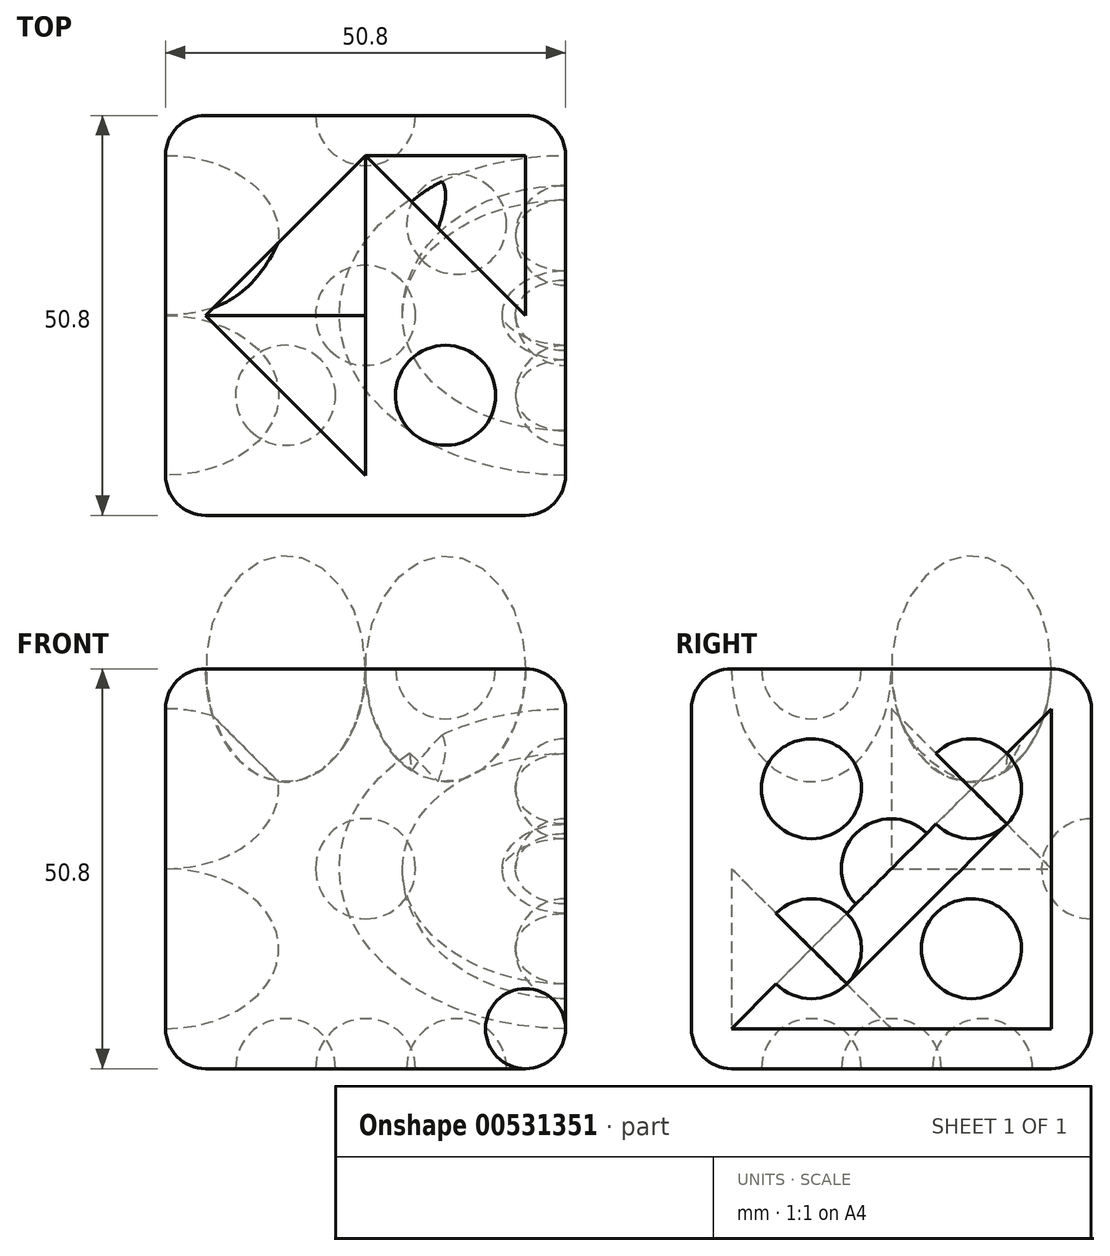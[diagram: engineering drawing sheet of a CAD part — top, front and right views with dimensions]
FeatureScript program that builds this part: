
annotation { "Feature Type Name" : "Feature", "Feature Type Description" : "" }
export const myFeature = defineFeature(function(context is Context, id is Id, definition is map)
    precondition{}
    {
        {
            var Q0;
            Q0=qCreatedBy(makeId("Front.planeOp"),FACE);
            var sketch = newSketch(context, id + "F0", { "sketchPlane" : qUnion([Q0])});
            skLineSegment(sketch, "E0", {"start": v(0, 0) * mm, "end": v(50.8, 0) * mm});
            skLineSegment(sketch, "E1", {"start": v(50.8, 0) * mm, "end": v(50.8, 50.8) * mm});
            skLineSegment(sketch, "E2", {"start": v(50.8, 50.8) * mm, "end": v(0, 50.8) * mm});
            skLineSegment(sketch, "E3", {"start": v(0, 50.8) * mm, "end": v(0, 0) * mm});
            skSolve(sketch);
        }
        {
            var Q0;
            Q0 = qSketchRegion(id + "F0", true);
            extrude(context, id + "F1", {"entities" : qUnion([Q0]), "depth" : 50.8 * mm, "offsetDistance" : 25.4 * mm});
        }
        {
            var Q0;
            Q0=makeQuery(id+"F1.opExtrude","CAP_EDGE",EDGE,{"disambiguationData":[OSD([sQuery(id+"F0.wireOp",EDGE,"E2")])],"isStart":false});
            var Q1;
            Q1=makeQuery(id+"F1.opExtrude","SWEPT_EDGE",EDGE,{"disambiguationData":[OSD([sQuery(id+"F0.wireOp",EDGE,"E1"),sQuery(id+"F0.wireOp",EDGE,"E2")])]});
            var Q2;
            Q2=makeQuery(id+"F1.opExtrude","CAP_EDGE",EDGE,{"disambiguationData":[OSD([sQuery(id+"F0.wireOp",EDGE,"E0")])],"isStart":false});
            var Q3;
            Q3=makeQuery(id+"F1.opExtrude","SWEPT_EDGE",EDGE,{"disambiguationData":[OSD([sQuery(id+"F0.wireOp",EDGE,"E0"),sQuery(id+"F0.wireOp",EDGE,"E1")])]});
            var Q4;
            Q4=makeQuery(id+"F1.opExtrude","CAP_EDGE",EDGE,{"disambiguationData":[OSD([sQuery(id+"F0.wireOp",EDGE,"E1")])],"isStart":false});
            var Q5;
            Q5=makeQuery(id+"F1.opExtrude","CAP_EDGE",EDGE,{"disambiguationData":[OSD([sQuery(id+"F0.wireOp",EDGE,"E1")])],"isStart":true});
            var Q6;
            Q6=makeQuery(id+"F1.opExtrude","CAP_EDGE",EDGE,{"disambiguationData":[OSD([sQuery(id+"F0.wireOp",EDGE,"E3")])],"isStart":false});
            var Q7;
            Q7=makeQuery(id+"F1.opExtrude","SWEPT_EDGE",EDGE,{"disambiguationData":[OSD([sQuery(id+"F0.wireOp",EDGE,"E2"),sQuery(id+"F0.wireOp",EDGE,"E3")])]});
            var Q8;
            Q8=makeQuery(id+"F1.opExtrude","CAP_EDGE",EDGE,{"disambiguationData":[OSD([sQuery(id+"F0.wireOp",EDGE,"E2")])],"isStart":true});
            var Q9;
            Q9=makeQuery(id+"F1.opExtrude","CAP_EDGE",EDGE,{"disambiguationData":[OSD([sQuery(id+"F0.wireOp",EDGE,"E3")])],"isStart":true});
            var Q10;
            Q10=makeQuery(id+"F1.opExtrude","SWEPT_EDGE",EDGE,{"disambiguationData":[OSD([sQuery(id+"F0.wireOp",EDGE,"E0"),sQuery(id+"F0.wireOp",EDGE,"E3")])]});
            var Q11;
            Q11=makeQuery(id+"F1.opExtrude","CAP_EDGE",EDGE,{"disambiguationData":[OSD([sQuery(id+"F0.wireOp",EDGE,"E0")])],"isStart":true});
            fillet(context, id + "F2", {"entities" : qUnion([Q0, Q1, Q2, Q3, Q4, Q5, Q6, Q7, Q8, Q9, Q10, Q11]), "radius" : 5.08 * mm, "tangentPropagation" : true, "allowEdgeOverflow" : false});
        }
        {
            var Q0;
            Q0=makeQuery(id+"F1.opExtrude","CAP_FACE",FACE,{"disambiguationData":[OSD([sQuery(id+"F0.wireOp",EDGE,"E0"),sQuery(id+"F0.wireOp",EDGE,"E1"),sQuery(id+"F0.wireOp",EDGE,"E2"),sQuery(id+"F0.wireOp",EDGE,"E3")])],"isStart":false});
            var sketch = newSketch(context, id + "F3", { "sketchPlane" : qUnion([Q0])});
            skLineSegment(sketch, "E4", {"start": v(5.08, 45.72) * mm, "end": v(45.72, 5.08) * mm});
            skLineSegment(sketch, "E5", {"start": v(5.08, 5.08) * mm, "end": v(45.72, 45.72) * mm});
            skLineSegment(sketch, "E6", {"start": v(25.4, 45.72) * mm, "end": v(25.4, 5.08) * mm});
            skLineSegment(sketch, "E7", {"start": v(5.08, 25.4) * mm, "end": v(45.72, 25.4) * mm});
            skLineSegment(sketch, "E8", {"start": v(5.08, 25.4) * mm, "end": v(25.4, 45.72) * mm});
            skLineSegment(sketch, "E9", {"start": v(25.4, 45.72) * mm, "end": v(45.72, 25.4) * mm});
            skLineSegment(sketch, "E10", {"start": v(5.08, 25.4) * mm, "end": v(25.4, 5.08) * mm});
            skLineSegment(sketch, "E11", {"start": v(45.72, 25.4) * mm, "end": v(25.4, 5.08) * mm});
            skCircle(sketch, "E12", {"center": v(25.4, 25.4) * mm, "radius": 6.35 * mm});
            skSolve(sketch);
        }
        {
            var Q0;
            Q0=makeQuery(id+"F1.opExtrude","SWEPT_FACE",FACE,{"disambiguationData":[OSD([sQuery(id+"F0.wireOp",EDGE,"E3")])]});
            var sketch = newSketch(context, id + "F4", { "sketchPlane" : qUnion([Q0])});
            skLineSegment(sketch, "E13", {"start": v(5.08, 45.72) * mm, "end": v(45.72, 5.08) * mm});
            skLineSegment(sketch, "E14", {"start": v(5.08, 5.08) * mm, "end": v(45.72, 45.72) * mm});
            skLineSegment(sketch, "E15", {"start": v(5.08, 25.4) * mm, "end": v(45.72, 25.4) * mm});
            skLineSegment(sketch, "E16", {"start": v(25.4, 45.72) * mm, "end": v(25.4, 5.08) * mm});
            skLineSegment(sketch, "E17", {"start": v(5.08, 25.4) * mm, "end": v(25.4, 45.72) * mm});
            skLineSegment(sketch, "E18", {"start": v(25.4, 5.08) * mm, "end": v(45.72, 25.4) * mm});
            skCircle(sketch, "E19", {"center": v(15.24, 35.56) * mm, "radius": 6.35 * mm});
            skCircle(sketch, "E20", {"center": v(35.56, 15.24) * mm, "radius": 6.35 * mm});
            skSolve(sketch);
        }
        {
            var Q0;
            {var subQ0=sQuery(id+"F4.wireOp",EDGE,"E19");var subQ1=sQuery(id+"F4.wireOp",EDGE,"E13");var subQ2=makeQuery(id+"F4.imprint","INTERSECT",VERTEX,{"disambiguationData":[OD(0.0)],"derivedFrom":[subQ1,subQ0]});Q0=makeQuery(id+"F4.imprint","IMPRINT",FACE,{"disambiguationData":[TD([[makeQuery(id+"F4.imprint","IMPRINT",EDGE,{"disambiguationData":[TD([[subQ2,-1.0]])],"derivedFrom":subQ1}),1.0]])]});}
            var Q1;
            {var subQ0=sQuery(id+"F4.wireOp",EDGE,"E17");var subQ1=sQuery(id+"F4.wireOp",EDGE,"E13");var subQ2=makeQuery(id+"F4.imprint","INTERSECT",VERTEX,{"derivedFrom":[subQ1,subQ0]});Q1=makeQuery(id+"F4.imprint","IMPRINT",FACE,{"disambiguationData":[TD([[makeQuery(id+"F4.imprint","IMPRINT",EDGE,{"disambiguationData":[TD([[subQ2,-1.0]])],"derivedFrom":subQ1}),1.0]])]});}
            var Q2;
            {var subQ0=sQuery(id+"F4.wireOp",EDGE,"E20");var subQ1=sQuery(id+"F4.wireOp",EDGE,"E13");var subQ2=makeQuery(id+"F4.imprint","INTERSECT",VERTEX,{"disambiguationData":[OD(0.0)],"derivedFrom":[subQ1,subQ0]});Q2=makeQuery(id+"F4.imprint","IMPRINT",FACE,{"disambiguationData":[TD([[makeQuery(id+"F4.imprint","IMPRINT",EDGE,{"disambiguationData":[TD([[subQ2,-1.0]])],"derivedFrom":subQ1}),1.0]])]});}
            var Q3;
            {var subQ0=sQuery(id+"F4.wireOp",EDGE,"E18");var subQ1=sQuery(id+"F4.wireOp",EDGE,"E13");var subQ2=makeQuery(id+"F4.imprint","INTERSECT",VERTEX,{"derivedFrom":[subQ1,subQ0]});Q3=makeQuery(id+"F4.imprint","IMPRINT",FACE,{"disambiguationData":[TD([[makeQuery(id+"F4.imprint","IMPRINT",EDGE,{"disambiguationData":[TD([[subQ2,-1.0]])],"derivedFrom":subQ1}),1.0]])]});}
            var Q4;
            Q4=sQuery(id+"F4.wireOp",EDGE,"E13");
            revolve(context, id + "F5", {"operationType" : NewBodyOperationType.REMOVE, "entities" : qUnion([Q0, Q1, Q2, Q3]), "axis" : qUnion([Q4]), "revolveType" : RevolveType.FULL, "oppositeDirection" : true});
        }
        {
            var Q0;
            Q0=makeQuery(id+"F1.opExtrude","SWEPT_FACE",FACE,{"disambiguationData":[OSD([sQuery(id+"F0.wireOp",EDGE,"E0")])]});
            var sketch = newSketch(context, id + "F6", { "sketchPlane" : qUnion([Q0])});
            skLineSegment(sketch, "E21", {"start": v(5.08, 45.72) * mm, "end": v(45.72, 5.08) * mm});
            skCircle(sketch, "E22", {"center": v(15.24, 35.56) * mm, "radius": 6.35 * mm});
            skCircle(sketch, "E23", {"center": v(25.4, 25.4) * mm, "radius": 6.35 * mm});
            skCircle(sketch, "E24", {"center": v(36.97, 13.83) * mm, "radius": 6.35 * mm});
            skSolve(sketch);
        }
        {
            var Q0;
            {var subQ0=sQuery(id+"F6.wireOp",EDGE,"E22");var subQ1=sQuery(id+"F6.wireOp",EDGE,"E21");var subQ2=makeQuery(id+"F6.imprint","INTERSECT",VERTEX,{"disambiguationData":[OD(0.0)],"derivedFrom":[subQ1,subQ0]});Q0=makeQuery(id+"F6.imprint","IMPRINT",FACE,{"disambiguationData":[TD([[makeQuery(id+"F6.imprint","IMPRINT",EDGE,{"disambiguationData":[TD([[subQ2,-1.0]])],"derivedFrom":subQ1}),-1.0]])]});}
            var Q1;
            {var subQ0=sQuery(id+"F6.wireOp",EDGE,"E23");var subQ1=sQuery(id+"F6.wireOp",EDGE,"E21");var subQ2=makeQuery(id+"F6.imprint","INTERSECT",VERTEX,{"disambiguationData":[OD(0.0)],"derivedFrom":[subQ1,subQ0]});Q1=makeQuery(id+"F6.imprint","IMPRINT",FACE,{"disambiguationData":[TD([[makeQuery(id+"F6.imprint","IMPRINT",EDGE,{"disambiguationData":[TD([[subQ2,-1.0]])],"derivedFrom":subQ1}),-1.0]])]});}
            var Q2;
            {var subQ0=sQuery(id+"F6.wireOp",EDGE,"E24");var subQ1=sQuery(id+"F6.wireOp",EDGE,"E21");var subQ2=makeQuery(id+"F6.imprint","INTERSECT",VERTEX,{"disambiguationData":[OD(0.0)],"derivedFrom":[subQ1,subQ0]});Q2=makeQuery(id+"F6.imprint","IMPRINT",FACE,{"disambiguationData":[TD([[makeQuery(id+"F6.imprint","IMPRINT",EDGE,{"disambiguationData":[TD([[subQ2,-1.0]])],"derivedFrom":subQ1}),-1.0]])]});}
            var Q3;
            Q3=sQuery(id+"F6.wireOp",EDGE,"E21");
            revolve(context, id + "F7", {"operationType" : NewBodyOperationType.REMOVE, "entities" : qUnion([Q0, Q1, Q2]), "axis" : qUnion([Q3]), "revolveType" : RevolveType.FULL, "oppositeDirection" : true});
        }
        {
            var Q0;
            Q0=makeQuery(id+"F1.opExtrude","SWEPT_FACE",FACE,{"disambiguationData":[OSD([sQuery(id+"F0.wireOp",EDGE,"E2")])]});
            var sketch = newSketch(context, id + "F8", { "sketchPlane" : qUnion([Q0])});
            skLineSegment(sketch, "E25", {"start": v(5.08, -5.08) * mm, "end": v(45.72, -45.72) * mm});
            skLineSegment(sketch, "E26", {"start": v(5.08, -45.72) * mm, "end": v(45.72, -5.08) * mm});
            skLineSegment(sketch, "E27", {"start": v(25.4, -5.08) * mm, "end": v(25.4, -45.72) * mm});
            skLineSegment(sketch, "E28", {"start": v(5.08, -25.4) * mm, "end": v(45.72, -25.4) * mm});
            skLineSegment(sketch, "E29", {"start": v(25.4, -5.08) * mm, "end": v(45.72, -25.4) * mm});
            skLineSegment(sketch, "E30", {"start": v(45.72, -25.4) * mm, "end": v(25.4, -45.72) * mm});
            skLineSegment(sketch, "E31", {"start": v(5.08, -25.4) * mm, "end": v(25.4, -45.72) * mm});
            skLineSegment(sketch, "E32", {"start": v(5.08, -25.4) * mm, "end": v(25.4, -5.08) * mm});
            skCircle(sketch, "E33", {"center": v(15.24, -15.24) * mm, "radius": 6.35 * mm});
            skCircle(sketch, "E34", {"center": v(35.56, -15.24) * mm, "radius": 6.35 * mm});
            skCircle(sketch, "E35", {"center": v(15.24, -35.56) * mm, "radius": 6.35 * mm});
            skCircle(sketch, "E36", {"center": v(35.56, -35.56) * mm, "radius": 6.35 * mm});
            skSolve(sketch);
        }
        {
            var Q0;
            {var subQ0=sQuery(id+"F8.wireOp",EDGE,"E33");var subQ1=sQuery(id+"F8.wireOp",EDGE,"E25");var subQ2=makeQuery(id+"F8.imprint","INTERSECT",VERTEX,{"disambiguationData":[OD(0.0)],"derivedFrom":[subQ1,subQ0]});Q0=makeQuery(id+"F8.imprint","IMPRINT",FACE,{"disambiguationData":[TD([[makeQuery(id+"F8.imprint","IMPRINT",EDGE,{"disambiguationData":[TD([[subQ2,-1.0]])],"derivedFrom":subQ1}),1.0]])]});}
            var Q1;
            {var subQ0=sQuery(id+"F8.wireOp",EDGE,"E32");var subQ1=sQuery(id+"F8.wireOp",EDGE,"E25");var subQ2=makeQuery(id+"F8.imprint","INTERSECT",VERTEX,{"derivedFrom":[subQ1,subQ0]});Q1=makeQuery(id+"F8.imprint","IMPRINT",FACE,{"disambiguationData":[TD([[makeQuery(id+"F8.imprint","IMPRINT",EDGE,{"disambiguationData":[TD([[subQ2,-1.0]])],"derivedFrom":subQ1}),1.0]])]});}
            var Q2;
            {var subQ0=sQuery(id+"F8.wireOp",EDGE,"E36");var subQ1=sQuery(id+"F8.wireOp",EDGE,"E25");var subQ2=makeQuery(id+"F8.imprint","INTERSECT",VERTEX,{"disambiguationData":[OD(0.0)],"derivedFrom":[subQ1,subQ0]});Q2=makeQuery(id+"F8.imprint","IMPRINT",FACE,{"disambiguationData":[TD([[makeQuery(id+"F8.imprint","IMPRINT",EDGE,{"disambiguationData":[TD([[subQ2,-1.0]])],"derivedFrom":subQ1}),1.0]])]});}
            var Q3;
            {var subQ0=sQuery(id+"F8.wireOp",EDGE,"E30");var subQ1=sQuery(id+"F8.wireOp",EDGE,"E25");var subQ2=makeQuery(id+"F8.imprint","INTERSECT",VERTEX,{"derivedFrom":[subQ1,subQ0]});Q3=makeQuery(id+"F8.imprint","IMPRINT",FACE,{"disambiguationData":[TD([[makeQuery(id+"F8.imprint","IMPRINT",EDGE,{"disambiguationData":[TD([[subQ2,-1.0]])],"derivedFrom":subQ1}),1.0]])]});}
            var Q4;
            Q4=sQuery(id+"F8.wireOp",EDGE,"E25");
            revolve(context, id + "F9", {"operationType" : NewBodyOperationType.REMOVE, "entities" : qUnion([Q0, Q1, Q2, Q3]), "axis" : qUnion([Q4]), "revolveType" : RevolveType.FULL, "oppositeDirection" : true});
        }
        {
            var Q0;
            Q0=makeQuery(id+"F1.opExtrude","CAP_FACE",FACE,{"disambiguationData":[OSD([sQuery(id+"F0.wireOp",EDGE,"E0"),sQuery(id+"F0.wireOp",EDGE,"E1"),sQuery(id+"F0.wireOp",EDGE,"E2"),sQuery(id+"F0.wireOp",EDGE,"E3")])],"isStart":true});
            var sketch = newSketch(context, id + "F10", { "sketchPlane" : qUnion([Q0])});
            skLineSegment(sketch, "E37", {"start": v(-25.4, 45.72) * mm, "end": v(-25.4, 31.75) * mm});
            skArc(sketch, "E38", {"start": v(-31.75, 25.4) * mm, "mid": v(-25.4, 19.05) * mm, "end": v(-19.05, 25.4) * mm});
            skLineSegment(sketch, "E39", {"start": v(-5.08, 25.4) * mm, "end": v(-45.72, 25.4) * mm});
            skLineSegment(sketch, "E40.trimOffspring", {"start": v(-25.4, 19.05) * mm, "end": v(-25.4, 5.08) * mm});
            skSolve(sketch);
        }
        {
            var Q0;
            {var subQ0=sQuery(id+"F10.wireOp",EDGE,"E39");var subQ1=sQuery(id+"F10.wireOp",EDGE,"E38");var subQ2=makeQuery(id+"F10.imprint","INTERSECT",VERTEX,{"disambiguationData":[OD(0.0)],"derivedFrom":[subQ1,subQ0]});Q0=makeQuery(id+"F10.imprint","IMPRINT",FACE,{"disambiguationData":[TD([[makeQuery(id+"F10.imprint","IMPRINT",EDGE,{"disambiguationData":[TD([[subQ2,-1.0]])],"derivedFrom":subQ1}),1.0]])]});}
            var Q1;
            Q1=sQuery(id+"F10.wireOp",EDGE,"E39");
            revolve(context, id + "F11", {"operationType" : NewBodyOperationType.REMOVE, "entities" : qUnion([Q0]), "axis" : qUnion([Q1]), "revolveType" : RevolveType.FULL, "oppositeDirection" : true});
        }
        {
            var Q0;
            Q0=makeQuery(id+"F1.opExtrude","SWEPT_FACE",FACE,{"disambiguationData":[OSD([sQuery(id+"F0.wireOp",EDGE,"E1")])]});
            var sketch = newSketch(context, id + "F12", { "sketchPlane" : qUnion([Q0])});
            skLineSegment(sketch, "E41", {"start": v(-45.72, 45.72) * mm, "end": v(-5.08, 5.08) * mm});
            skLineSegment(sketch, "E42", {"start": v(-45.72, 5.08) * mm, "end": v(-5.08, 45.72) * mm});
            skCircle(sketch, "E43", {"center": v(-25.4, 25.4) * mm, "radius": 6.35 * mm});
            skCircle(sketch, "E44", {"center": v(-35.56, 35.56) * mm, "radius": 6.35 * mm});
            skCircle(sketch, "E45", {"center": v(-15.24, 35.56) * mm, "radius": 6.35 * mm});
            skCircle(sketch, "E46", {"center": v(-35.56, 15.24) * mm, "radius": 6.35 * mm});
            skCircle(sketch, "E47", {"center": v(-15.24, 15.24) * mm, "radius": 6.35 * mm});
            skSolve(sketch);
        }
        {
            var Q0;
            {var subQ0=sQuery(id+"F12.wireOp",EDGE,"E44");var subQ1=sQuery(id+"F12.wireOp",EDGE,"E41");var subQ2=makeQuery(id+"F12.imprint","INTERSECT",VERTEX,{"disambiguationData":[OD(0.0)],"derivedFrom":[subQ1,subQ0]});Q0=makeQuery(id+"F12.imprint","IMPRINT",FACE,{"disambiguationData":[TD([[makeQuery(id+"F12.imprint","IMPRINT",EDGE,{"disambiguationData":[TD([[subQ2,-1.0]])],"derivedFrom":subQ1}),1.0]])]});}
            var Q1;
            {var subQ0=sQuery(id+"F12.wireOp",EDGE,"E43");var subQ1=sQuery(id+"F12.wireOp",EDGE,"E41");var subQ2=makeQuery(id+"F12.imprint","INTERSECT",VERTEX,{"disambiguationData":[OD(0.0)],"derivedFrom":[subQ1,subQ0]});Q1=makeQuery(id+"F12.imprint","IMPRINT",FACE,{"disambiguationData":[TD([[makeQuery(id+"F12.imprint","IMPRINT",EDGE,{"disambiguationData":[TD([[subQ2,-1.0]])],"derivedFrom":subQ1}),1.0]])]});}
            var Q2;
            {var subQ0=sQuery(id+"F12.wireOp",EDGE,"E42");var subQ1=sQuery(id+"F12.wireOp",EDGE,"E41");var subQ2=makeQuery(id+"F12.imprint","INTERSECT",VERTEX,{"derivedFrom":[subQ1,subQ0]});Q2=makeQuery(id+"F12.imprint","IMPRINT",FACE,{"disambiguationData":[TD([[makeQuery(id+"F12.imprint","IMPRINT",EDGE,{"disambiguationData":[TD([[subQ2,-1.0]])],"derivedFrom":subQ1}),1.0]])]});}
            var Q3;
            {var subQ0=sQuery(id+"F12.wireOp",EDGE,"E47");var subQ1=sQuery(id+"F12.wireOp",EDGE,"E41");var subQ2=makeQuery(id+"F12.imprint","INTERSECT",VERTEX,{"disambiguationData":[OD(0.0)],"derivedFrom":[subQ1,subQ0]});Q3=makeQuery(id+"F12.imprint","IMPRINT",FACE,{"disambiguationData":[TD([[makeQuery(id+"F12.imprint","IMPRINT",EDGE,{"disambiguationData":[TD([[subQ2,-1.0]])],"derivedFrom":subQ1}),1.0]])]});}
            var Q4;
            Q4=sQuery(id+"F12.wireOp",EDGE,"E41");
            revolve(context, id + "F13", {"operationType" : NewBodyOperationType.REMOVE, "entities" : qUnion([Q0, Q1, Q2, Q3]), "axis" : qUnion([Q4]), "revolveType" : RevolveType.FULL, "oppositeDirection" : true});
        }
        {
            var Q0;
            Q0=makeQuery(id+"F1.opExtrude","SWEPT_FACE",FACE,{"disambiguationData":[OSD([sQuery(id+"F0.wireOp",EDGE,"E1")])]});
            var sketch = newSketch(context, id + "F14", { "sketchPlane" : qUnion([Q0])});
            skLineSegment(sketch, "E48", {"start": v(-45.72, 5.08) * mm, "end": v(-5.08, 45.72) * mm});
            skLineSegment(sketch, "E49", {"start": v(-25.4, 45.72) * mm, "end": v(-5.08, 25.4) * mm});
            skLineSegment(sketch, "E50", {"start": v(-45.72, 25.4) * mm, "end": v(-25.4, 5.08) * mm});
            skCircle(sketch, "E51", {"center": v(-35.56, 15.24) * mm, "radius": 6.35 * mm});
            skCircle(sketch, "E52", {"center": v(-15.24, 35.56) * mm, "radius": 6.35 * mm});
            skSolve(sketch);
        }
        {
            var Q0;
            {var subQ0=sQuery(id+"F14.wireOp",EDGE,"E50");var subQ1=sQuery(id+"F14.wireOp",EDGE,"E48");var subQ2=makeQuery(id+"F14.imprint","INTERSECT",VERTEX,{"derivedFrom":[subQ1,subQ0]});Q0=makeQuery(id+"F14.imprint","IMPRINT",FACE,{"disambiguationData":[TD([[makeQuery(id+"F14.imprint","IMPRINT",EDGE,{"disambiguationData":[TD([[subQ2,-1.0]])],"derivedFrom":subQ1}),1.0]])]});}
            var Q1;
            {var subQ0=sQuery(id+"F14.wireOp",EDGE,"E51");var subQ1=sQuery(id+"F14.wireOp",EDGE,"E48");var subQ2=makeQuery(id+"F14.imprint","INTERSECT",VERTEX,{"disambiguationData":[OD(0.0)],"derivedFrom":[subQ1,subQ0]});Q1=makeQuery(id+"F14.imprint","IMPRINT",FACE,{"disambiguationData":[TD([[makeQuery(id+"F14.imprint","IMPRINT",EDGE,{"disambiguationData":[TD([[subQ2,-1.0]])],"derivedFrom":subQ1}),1.0]])]});}
            var Q2;
            {var subQ0=sQuery(id+"F14.wireOp",EDGE,"E52");var subQ1=sQuery(id+"F14.wireOp",EDGE,"E48");var subQ2=makeQuery(id+"F14.imprint","INTERSECT",VERTEX,{"disambiguationData":[OD(0.0)],"derivedFrom":[subQ1,subQ0]});Q2=makeQuery(id+"F14.imprint","IMPRINT",FACE,{"disambiguationData":[TD([[makeQuery(id+"F14.imprint","IMPRINT",EDGE,{"disambiguationData":[TD([[subQ2,-1.0]])],"derivedFrom":subQ1}),1.0]])]});}
            var Q3;
            {var subQ0=sQuery(id+"F14.wireOp",EDGE,"E49");var subQ1=sQuery(id+"F14.wireOp",EDGE,"E48");var subQ2=makeQuery(id+"F14.imprint","INTERSECT",VERTEX,{"derivedFrom":[subQ1,subQ0]});Q3=makeQuery(id+"F14.imprint","IMPRINT",FACE,{"disambiguationData":[TD([[makeQuery(id+"F14.imprint","IMPRINT",EDGE,{"disambiguationData":[TD([[subQ2,-1.0]])],"derivedFrom":subQ1}),1.0]])]});}
            var Q4;
            Q4=sQuery(id+"F14.wireOp",EDGE,"E48");
            revolve(context, id + "F15", {"operationType" : NewBodyOperationType.REMOVE, "entities" : qUnion([Q0, Q1, Q2, Q3]), "axis" : qUnion([Q4]), "revolveType" : RevolveType.FULL, "oppositeDirection" : true});
        }
        {
            var Q0;
            {var subQ0=sQuery(id+"F8.wireOp",EDGE,"E29");var subQ1=sQuery(id+"F8.wireOp",EDGE,"E26");var subQ2=makeQuery(id+"F8.imprint","INTERSECT",VERTEX,{"derivedFrom":[subQ1,subQ0]});Q0=makeQuery(id+"F8.imprint","IMPRINT",FACE,{"disambiguationData":[TD([[makeQuery(id+"F8.imprint","IMPRINT",EDGE,{"disambiguationData":[TD([[subQ2,-1.0]])],"derivedFrom":subQ1}),-1.0]])]});}
            var Q1;
            {var subQ0=sQuery(id+"F8.wireOp",EDGE,"E34");var subQ1=sQuery(id+"F8.wireOp",EDGE,"E26");var subQ2=makeQuery(id+"F8.imprint","INTERSECT",VERTEX,{"disambiguationData":[OD(0.0)],"derivedFrom":[subQ1,subQ0]});Q1=makeQuery(id+"F8.imprint","IMPRINT",FACE,{"disambiguationData":[TD([[makeQuery(id+"F8.imprint","IMPRINT",EDGE,{"disambiguationData":[TD([[subQ2,-1.0]])],"derivedFrom":subQ1}),-1.0]])]});}
            var Q2;
            {var subQ0=sQuery(id+"F8.wireOp",EDGE,"E31");var subQ1=sQuery(id+"F8.wireOp",EDGE,"E26");var subQ2=makeQuery(id+"F8.imprint","INTERSECT",VERTEX,{"derivedFrom":[subQ1,subQ0]});Q2=makeQuery(id+"F8.imprint","IMPRINT",FACE,{"disambiguationData":[TD([[makeQuery(id+"F8.imprint","IMPRINT",EDGE,{"disambiguationData":[TD([[subQ2,-1.0]])],"derivedFrom":subQ1}),-1.0]])]});}
            var Q3;
            {var subQ0=sQuery(id+"F8.wireOp",EDGE,"E35");var subQ1=sQuery(id+"F8.wireOp",EDGE,"E26");var subQ2=makeQuery(id+"F8.imprint","INTERSECT",VERTEX,{"disambiguationData":[OD(0.0)],"derivedFrom":[subQ1,subQ0]});Q3=makeQuery(id+"F8.imprint","IMPRINT",FACE,{"disambiguationData":[TD([[makeQuery(id+"F8.imprint","IMPRINT",EDGE,{"disambiguationData":[TD([[subQ2,-1.0]])],"derivedFrom":subQ1}),-1.0]])]});}
            var Q4;
            Q4=sQuery(id+"F8.wireOp",EDGE,"E26");
            revolve(context, id + "F16", {"operationType" : NewBodyOperationType.REMOVE, "entities" : qUnion([Q0, Q1, Q2, Q3]), "axis" : qUnion([Q4]), "revolveType" : RevolveType.FULL, "oppositeDirection" : true});
        }
    });
